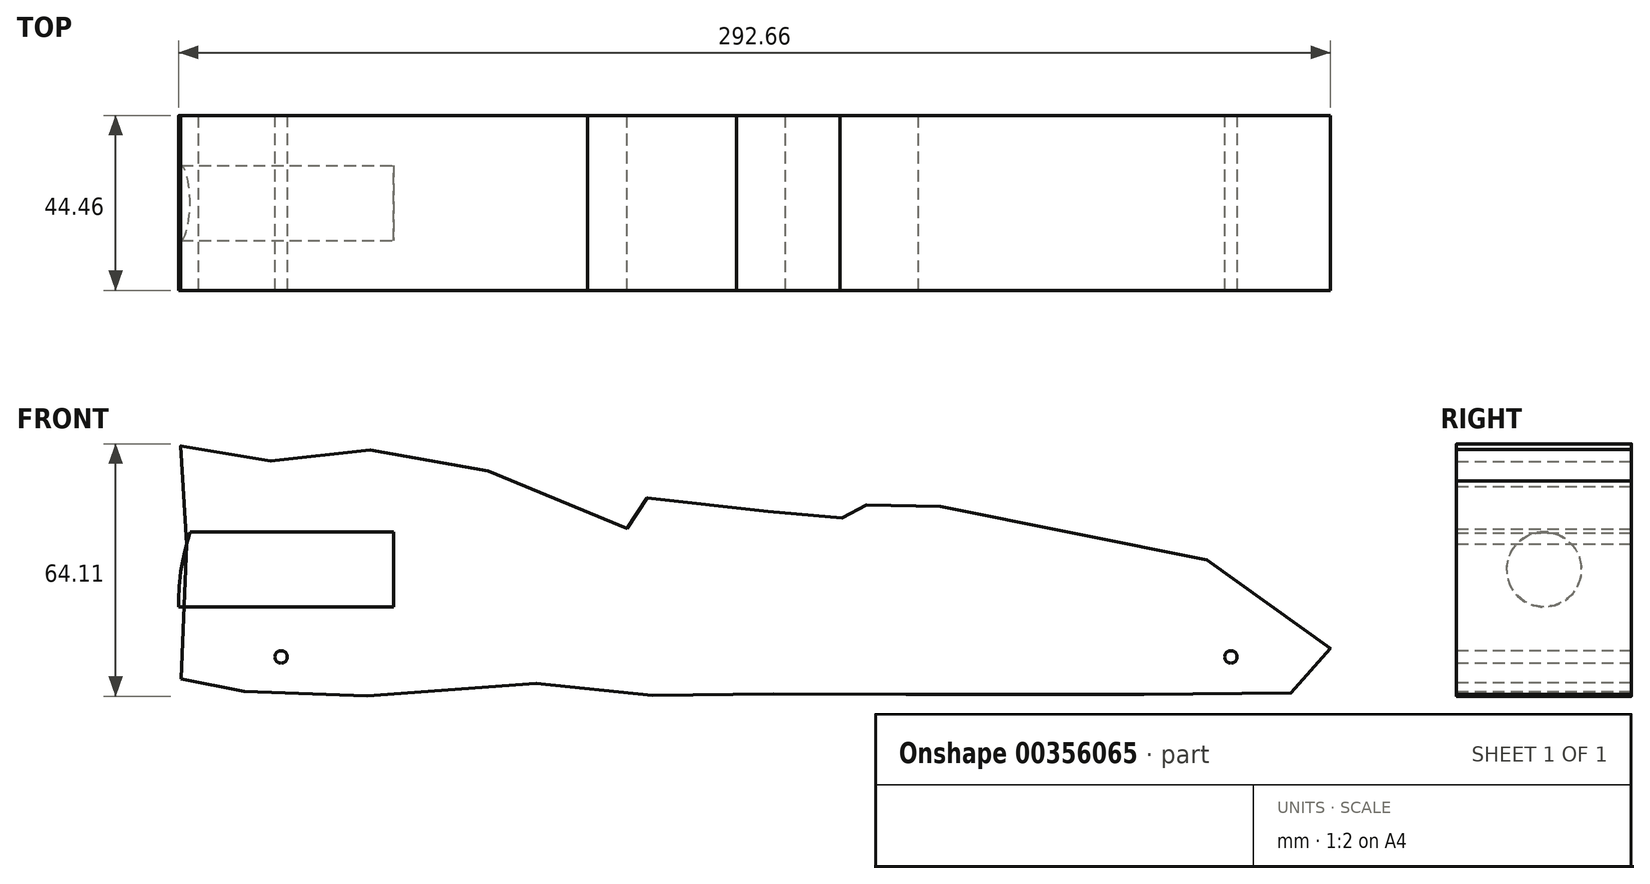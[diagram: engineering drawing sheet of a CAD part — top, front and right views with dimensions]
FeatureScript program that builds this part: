
annotation { "Feature Type Name" : "Feature", "Feature Type Description" : "" }
export const myFeature = defineFeature(function(context is Context, id is Id, definition is map)
    precondition{}
    {
        {
            var Q0;
            Q0=qCreatedBy(makeId("Front.planeOp"),FACE);
            var sketch = newSketch(context, id + "F0", { "sketchPlane" : qUnion([Q0])});
            skLineSegment(sketch, "E0.bottom", {"start": v(-146.05, 31.75) * mm, "end": v(146.05, 31.75) * mm, "construction": true});
            skLineSegment(sketch, "E0.top", {"start": v(-146.05, -31.75) * mm, "end": v(146.05, -31.75) * mm, "construction": true});
            skLineSegment(sketch, "E0.right", {"start": v(146.05, 31.75) * mm, "end": v(146.05, -31.75) * mm, "construction": true});
            skFitSpline(sketch, "E1", {"points": [v(-146.05, -27.8) * mm, v(-146.05, 0) * mm, v(-142.06, 24.15) * mm, v(-146.05, 31.75) * mm, v(-130.85, 28.01) * mm, v(-118.11, 28.36) * mm, v(-99.54, 30.48) * mm, v(-94.38, 29.83) * mm, v(-57.37, 21.68) * mm, v(-32.98, 10.64) * mm, v(-42.64, 20.76) * mm, v(7.5, 9.72) * mm, v(-4.91, 22.14) * mm, v(41.1, 6.5) * mm, v(21.77, 21.23) * mm, v(73.3, 9.26) * mm, v(143.15, -10.27) * mm, v(145.27, -29.73) * mm, v(145.06, -30.28) * mm, v(144.44, -30.68) * mm, v(115.32, -31.72) * mm, v(90.85, -31.75) * mm, v(68.27, -31.75) * mm, v(46.77, -31.75) * mm, v(19.12, -31.75) * mm, v(-7.07, -31.75) * mm, v(-27.86, -31.75) * mm, v(-40.94, -28.86) * mm, v(-90.82, -31.75) * mm, v(-109.77, -31.75) * mm, v(-138.38, -31.3) * mm, v(-146.05, -31.75) * mm, v(-146.05, -27.8) * mm]});
            skLineSegment(sketch, "E2.bottom", {"start": v(-146.05, 9.52) * mm, "end": v(-95.25, 9.52) * mm, "construction": true});
            skLineSegment(sketch, "E2.top", {"start": v(-141.83, -9.52) * mm, "end": v(-95.25, -9.52) * mm, "construction": true});
            skLineSegment(sketch, "E2.right", {"start": v(-95.25, 9.52) * mm, "end": v(-95.25, -9.52) * mm, "construction": true});
            skLineSegment(sketch, "E3", {"start": v(-146.05, 31.75) * mm, "end": v(-146.05, -31.75) * mm, "construction": true});
            skSolve(sketch);
        }
        {
            var Q0;
            Q0=qCreatedBy(makeId("Right.planeOp"),FACE);
            var sketch = newSketch(context, id + "F1", { "sketchPlane" : qUnion([Q0])});
            skCircle(sketch, "E4", {"center": v(0, 0) * mm, "radius": 9.53 * mm});
            skSolve(sketch);
        }
        {
            var Q0;
            Q0=qCreatedBy(makeId("Front.planeOp"),FACE);
            var sketch = newSketch(context, id + "F2", { "sketchPlane" : qUnion([Q0])});
            skCircle(sketch, "E5", {"center": v(-120.65, -22.22) * mm, "radius": 1.59 * mm});
            skCircle(sketch, "E6", {"center": v(120.65, -22.23) * mm, "radius": 1.59 * mm});
            skSolve(sketch);
        }
        {
            var Q0;
            Q0=qSketchRegion(id+"F0",true);
            extrude(context, id + "F3", {"entities" : qUnion([Q0]), "depth" : 44.45 * mm, "symmetric" : true});
        }
        {
            var Q0;
            Q0=qSketchRegion(id+"F1",true);
            extrude(context, id + "F4", {"entities" : qUnion([Q0]), "operationType" : NewBodyOperationType.REMOVE, "oppositeDirection" : true, "depth" : 152.4 * mm, "hasSecondDirection" : true, "secondDirectionOppositeDirection" : true, "secondDirectionDepth" : 92.07 * mm});
        }
        {
            var Q0;
            Q0=qSketchRegion(id+"F2",true);
            extrude(context, id + "F5", {"entities" : qUnion([Q0]), "operationType" : NewBodyOperationType.REMOVE, "oppositeDirection" : true, "depth" : 50.8 * mm, "symmetric" : true});
        }
    });
